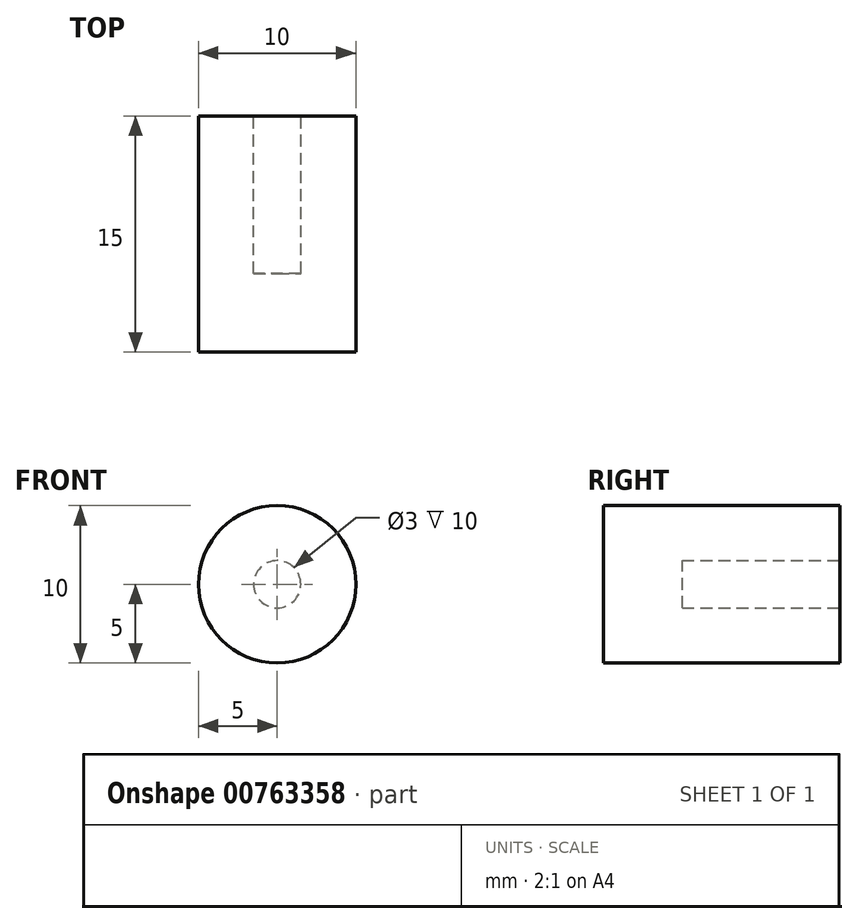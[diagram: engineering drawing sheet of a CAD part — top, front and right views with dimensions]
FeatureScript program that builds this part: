
annotation { "Feature Type Name" : "Feature", "Feature Type Description" : "" }
export const myFeature = defineFeature(function(context is Context, id is Id, definition is map)
    precondition{}
    {
        {
            var Q0;
            Q0=qCreatedBy(makeId("Front.planeOp"),FACE);
            var sketch = newSketch(context, id + "F0", { "sketchPlane" : qUnion([Q0])});
            skCircle(sketch, "E0", {"center": v(0, 0) * mm, "radius": 5 * mm});
            skCircle(sketch, "E1", {"center": v(0, 0) * mm, "radius": 1.5 * mm});
            skSolve(sketch);
        }
        {
            var Q0;
            Q0 = qSketchRegion(id + "F0", true);
            var Q1;
            Q1=makeQuery(id+"F0.imprint","IMPRINT",FACE,{"disambiguationData":[TD([[makeQuery(id+"F0.imprint","IMPRINT",EDGE,{"derivedFrom":sQuery(id+"F0.wireOp",EDGE,"E1")}),1.0]])]});
            extrude(context, id + "F1", {"entities" : qUnion([Q0, Q1]), "depth" : 15 * mm, "offsetDistance" : 25 * mm});
        }
        {
            var Q0;
            Q0=makeQuery(id+"F0.imprint","IMPRINT",FACE,{"disambiguationData":[TD([[makeQuery(id+"F0.imprint","IMPRINT",EDGE,{"derivedFrom":sQuery(id+"F0.wireOp",EDGE,"E1")}),1.0]])]});
            extrude(context, id + "F2", {"entities" : qUnion([Q0]), "operationType" : NewBodyOperationType.REMOVE, "oppositeDirection" : true, "depth" : -10 * mm, "offsetDistance" : 25 * mm});
        }
    });
